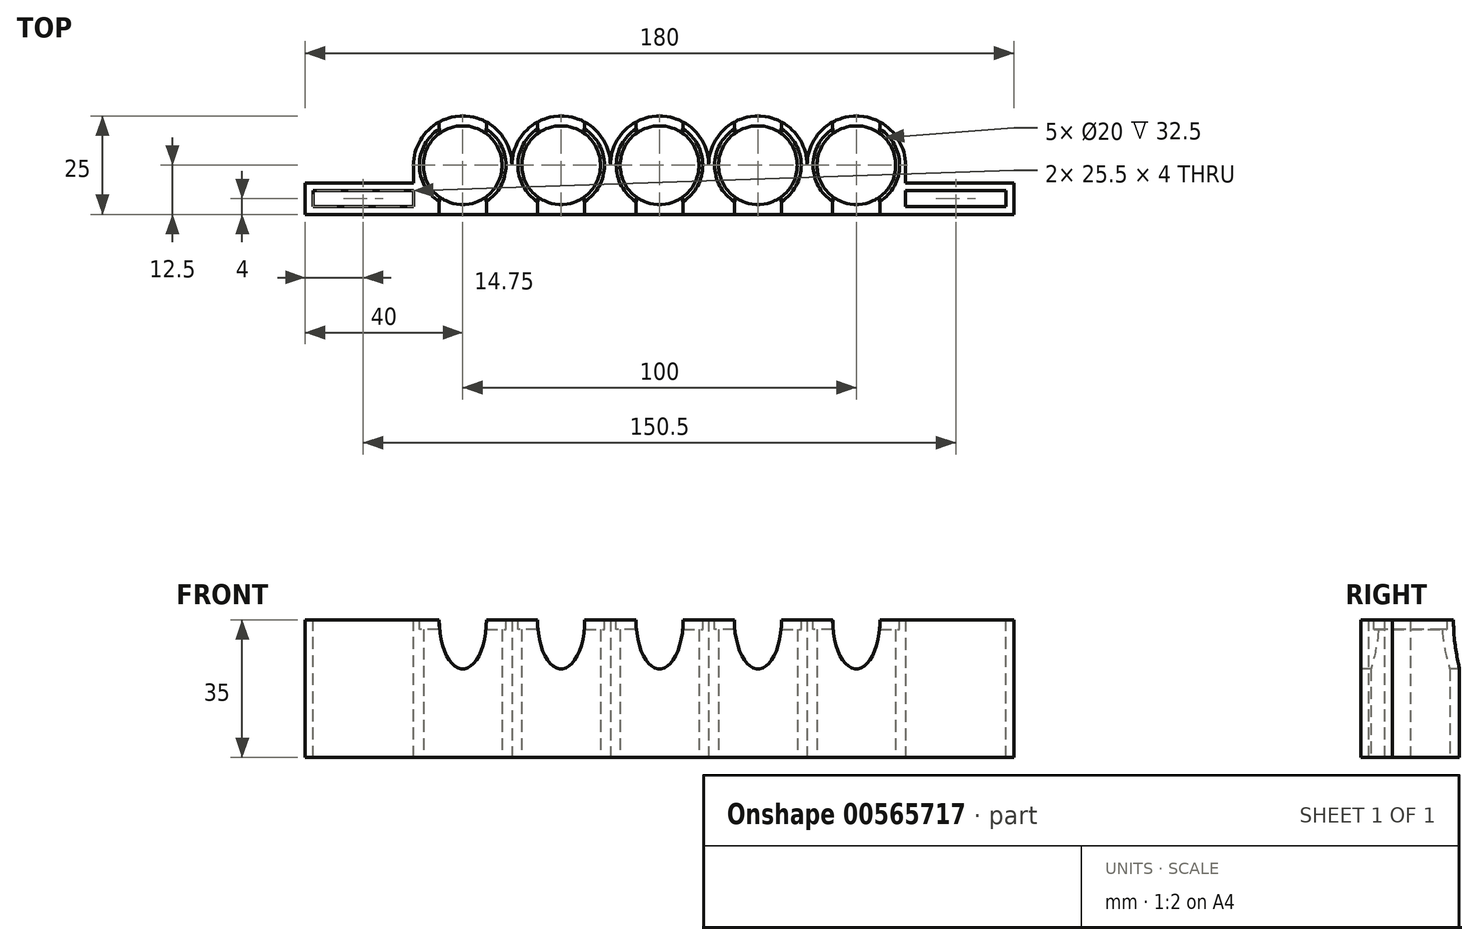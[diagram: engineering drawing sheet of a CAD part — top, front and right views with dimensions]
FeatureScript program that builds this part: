
annotation { "Feature Type Name" : "Feature", "Feature Type Description" : "" }
export const myFeature = defineFeature(function(context is Context, id is Id, definition is map)
    precondition{}
    {
        {
            var Q0;
            Q0=qCreatedBy(makeId("Top.planeOp"),FACE);
            var sketch = newSketch(context, id + "F0", { "sketchPlane" : qUnion([Q0])});
            skArc(sketch, "E0", {"start": v(12.5, 0) * mm, "mid": v(0, 12.5) * mm, "end": v(-12.5, 0) * mm});
            skArc(sketch, "E1.1.0.0", {"start": v(37.5, 0) * mm, "mid": v(25, 12.5) * mm, "end": v(12.5, 0) * mm});
            skArc(sketch, "E1.2.0.0", {"start": v(62.5, 0) * mm, "mid": v(50, 12.5) * mm, "end": v(37.5, 0) * mm});
            skArc(sketch, "E1.3.0.0", {"start": v(87.5, 0) * mm, "mid": v(75, 12.5) * mm, "end": v(62.5, 0) * mm});
            skArc(sketch, "E1.4.0.0", {"start": v(112.5, 0) * mm, "mid": v(100, 12.5) * mm, "end": v(87.5, 0) * mm});
            skLineSegment(sketch, "E1.direction1", {"start": v(0, 0) * mm, "end": v(25, 0) * mm, "construction": true});
            skLineSegment(sketch, "E2", {"start": v(-40, -12.5) * mm, "end": v(140, -12.5) * mm});
            skCircle(sketch, "E3", {"center": v(0, 0) * mm, "radius": 10 * mm});
            skCircle(sketch, "E4.1.0.0", {"center": v(25, 0) * mm, "radius": 10 * mm});
            skCircle(sketch, "E4.2.0.0", {"center": v(50, 0) * mm, "radius": 10 * mm});
            skCircle(sketch, "E4.3.0.0", {"center": v(75, 0) * mm, "radius": 10 * mm});
            skCircle(sketch, "E4.4.0.0", {"center": v(100, 0) * mm, "radius": 10 * mm});
            skLineSegment(sketch, "E5", {"start": v(-40, -12.5) * mm, "end": v(-40, -10.5) * mm});
            skLineSegment(sketch, "E6", {"start": v(-40, -10.5) * mm, "end": v(-12.5, -10.5) * mm});
            skLineSegment(sketch, "E7", {"start": v(140, -12.5) * mm, "end": v(140, -10.5) * mm});
            skLineSegment(sketch, "E8", {"start": v(140, -10.5) * mm, "end": v(112.5, -10.5) * mm});
            skPoint(sketch, "E9.orphan", {"position": v(0, -12.5) * mm});
            skLineSegment(sketch, "E10", {"start": v(-12.5, 0) * mm, "end": v(-12.5, -10.5) * mm});
            skLineSegment(sketch, "E11", {"start": v(112.5, 0) * mm, "end": v(112.5, -10.5) * mm});
            skPoint(sketch, "E12.orphan", {"position": v(100, -12.5) * mm});
            skSolve(sketch);
        }
        {
            var Q0;
            Q0 = qSketchRegion(id + "F0", true);
            extrude(context, id + "F1", {"entities" : qUnion([Q0]), "depth" : 35 * mm, "offsetDistance" : 25 * mm});
        }
        {
            var Q0;
            Q0=makeQuery(id+"F1.opExtrude","CAP_FACE",FACE,{"disambiguationData":[OSD([sQuery(id+"F0.wireOp",EDGE,"E0"),sQuery(id+"F0.wireOp",EDGE,"E1.1.0.0"),sQuery(id+"F0.wireOp",EDGE,"E1.2.0.0"),sQuery(id+"F0.wireOp",EDGE,"E1.3.0.0"),sQuery(id+"F0.wireOp",EDGE,"E1.4.0.0"),sQuery(id+"F0.wireOp",EDGE,"E2"),sQuery(id+"F0.wireOp",EDGE,"E3"),sQuery(id+"F0.wireOp",EDGE,"E4.1.0.0"),sQuery(id+"F0.wireOp",EDGE,"E4.2.0.0"),sQuery(id+"F0.wireOp",EDGE,"E4.3.0.0"),sQuery(id+"F0.wireOp",EDGE,"E4.4.0.0"),sQuery(id+"F0.wireOp",EDGE,"E5"),sQuery(id+"F0.wireOp",EDGE,"E6"),sQuery(id+"F0.wireOp",EDGE,"E7"),sQuery(id+"F0.wireOp",EDGE,"E8"),sQuery(id+"F0.wireOp",EDGE,"E10"),sQuery(id+"F0.wireOp",EDGE,"E11")])],"isStart":false});
            var sketch = newSketch(context, id + "F2", { "sketchPlane" : qUnion([Q0])});
            skCircle(sketch, "E13", {"center": v(0, 0) * mm, "radius": 11 * mm});
            skCircle(sketch, "E14.1.0.0", {"center": v(25, 0) * mm, "radius": 11 * mm});
            skCircle(sketch, "E14.2.0.0", {"center": v(50, 0) * mm, "radius": 11 * mm});
            skCircle(sketch, "E14.3.0.0", {"center": v(75, 0) * mm, "radius": 11 * mm});
            skCircle(sketch, "E14.4.0.0", {"center": v(100, 0) * mm, "radius": 11 * mm});
            skLineSegment(sketch, "E14.direction1", {"start": v(0, 0) * mm, "end": v(25, 0) * mm, "construction": true});
            skSolve(sketch);
        }
        {
            var Q0;
            Q0=makeQuery(id+"F2.imprint","IMPRINT",FACE,{"disambiguationData":[TD([[makeQuery(id+"F2.imprint","IMPRINT",EDGE,{"derivedFrom":sQuery(id+"F2.wireOp",EDGE,"E14.4.0.0")}),1.0]])]});
            var Q1;
            Q1=makeQuery(id+"F2.imprint","IMPRINT",FACE,{"disambiguationData":[TD([[makeQuery(id+"F2.imprint","IMPRINT",EDGE,{"derivedFrom":sQuery(id+"F2.wireOp",EDGE,"E14.3.0.0")}),1.0]])]});
            var Q2;
            Q2=makeQuery(id+"F2.imprint","IMPRINT",FACE,{"disambiguationData":[TD([[makeQuery(id+"F2.imprint","IMPRINT",EDGE,{"derivedFrom":makeQuery(id+"F1.opExtrude","CAP_EDGE",EDGE,{"disambiguationData":[OSD([sQuery(id+"F0.wireOp",EDGE,"E4.2.0.0")])],"isStart":false})}),1.0]])]});
            var Q3;
            Q3=makeQuery(id+"F2.imprint","IMPRINT",FACE,{"disambiguationData":[TD([[makeQuery(id+"F2.imprint","IMPRINT",EDGE,{"derivedFrom":sQuery(id+"F2.wireOp",EDGE,"E14.1.0.0")}),1.0]])]});
            var Q4;
            Q4=makeQuery(id+"F2.imprint","IMPRINT",FACE,{"disambiguationData":[TD([[makeQuery(id+"F2.imprint","IMPRINT",EDGE,{"derivedFrom":sQuery(id+"F2.wireOp",EDGE,"E13")}),1.0]])]});
            var Q5;
            Q5=makeQuery(id+"F2.imprint","IMPRINT",FACE,{"disambiguationData":[TD([[makeQuery(id+"F2.imprint","IMPRINT",EDGE,{"derivedFrom":sQuery(id+"F2.wireOp",EDGE,"E14.2.0.0")}),1.0]])]});
            var Q6;
            Q6=sQuery(id+"F2.wireOp",EDGE,"E14.4.0.0");
            extrude(context, id + "F3", {"entities" : qUnion([Q0, Q1, Q2, Q3, Q4, Q5]), "operationType" : NewBodyOperationType.REMOVE, "surfaceEntities" : qUnion([Q6]), "oppositeDirection" : true, "depth" : 2.5 * mm, "offsetDistance" : 25 * mm});
        }
        {
            var Q0;
            Q0=qCreatedBy(makeId("Front.planeOp"),FACE);
            var sketch = newSketch(context, id + "F4", { "sketchPlane" : qUnion([Q0])});
            skEllipse(sketch, "E15", {"center": v(0, 35) * mm, "majorRadius": 6 * mm, "minorRadius": 12.5 * mm, "majorAxis": v(-1, 0)});
            skEllipse(sketch, "E16.1.0.0", {"center": v(25, 35) * mm, "majorRadius": 6 * mm, "minorRadius": 12.5 * mm, "majorAxis": v(-1, 0)});
            skEllipse(sketch, "E16.2.0.0", {"center": v(50, 35) * mm, "majorRadius": 6 * mm, "minorRadius": 12.5 * mm, "majorAxis": v(-1, 0)});
            skEllipse(sketch, "E16.3.0.0", {"center": v(75, 35) * mm, "majorRadius": 6 * mm, "minorRadius": 12.5 * mm, "majorAxis": v(-1, 0)});
            skEllipse(sketch, "E16.4.0.0", {"center": v(100, 35) * mm, "majorRadius": 6 * mm, "minorRadius": 12.5 * mm, "majorAxis": v(-1, 0)});
            skLineSegment(sketch, "E16.direction1", {"start": v(0, 35) * mm, "end": v(25, 35) * mm, "construction": true});
            skSolve(sketch);
        }
        {
            var Q0;
            Q0=makeQuery(id+"F4.imprint","IMPRINT",FACE,{"disambiguationData":[TD([[makeQuery(id+"F4.imprint","IMPRINT",EDGE,{"derivedFrom":sQuery(id+"F4.wireOp",EDGE,"E15")}),1.0]])]});
            var Q1;
            Q1=makeQuery(id+"F4.imprint","IMPRINT",FACE,{"disambiguationData":[TD([[makeQuery(id+"F4.imprint","IMPRINT",EDGE,{"derivedFrom":sQuery(id+"F4.wireOp",EDGE,"E16.1.0.0")}),1.0]])]});
            var Q2;
            Q2=makeQuery(id+"F4.imprint","IMPRINT",FACE,{"disambiguationData":[TD([[makeQuery(id+"F4.imprint","IMPRINT",EDGE,{"derivedFrom":sQuery(id+"F4.wireOp",EDGE,"E16.2.0.0")}),1.0]])]});
            var Q3;
            Q3=makeQuery(id+"F4.imprint","IMPRINT",FACE,{"disambiguationData":[TD([[makeQuery(id+"F4.imprint","IMPRINT",EDGE,{"derivedFrom":sQuery(id+"F4.wireOp",EDGE,"E16.3.0.0")}),1.0]])]});
            var Q4;
            Q4=makeQuery(id+"F4.imprint","IMPRINT",FACE,{"disambiguationData":[TD([[makeQuery(id+"F4.imprint","IMPRINT",EDGE,{"derivedFrom":sQuery(id+"F4.wireOp",EDGE,"E16.4.0.0")}),1.0]])]});
            extrude(context, id + "F5", {"entities" : qUnion([Q0, Q1, Q2, Q3, Q4]), "operationType" : NewBodyOperationType.REMOVE, "endBound" : BoundingType.SYMMETRIC, "oppositeDirection" : true, "depth" : 50 * mm, "offsetDistance" : 25 * mm});
        }
        {
            var Q0;
            {var subQ0=sQuery(id+"F0.wireOp",EDGE,"E6");var subQ1=sQuery(id+"F0.wireOp",EDGE,"E5");var subQ2=sQuery(id+"F0.wireOp",EDGE,"E2");var subQ3=sQuery(id+"F0.wireOp",EDGE,"E0");var subQ4=sQuery(id+"F0.wireOp",EDGE,"E10");Q0=makeQuery(id+"F5.boolean.opBoolean","SPLIT",FACE,{"disambiguationData":[TD([makeQuery(id+"F1.opExtrude","SWEPT_FACE",FACE,{"disambiguationData":[OSD([subQ3])]}),makeQuery(id+"F1.opExtrude","SWEPT_FACE",FACE,{"disambiguationData":[OSD([subQ2])]}),makeQuery(id+"F1.opExtrude","SWEPT_FACE",FACE,{"disambiguationData":[OSD([subQ1])]}),makeQuery(id+"F1.opExtrude","SWEPT_FACE",FACE,{"disambiguationData":[OSD([subQ0])]}),makeQuery(id+"F1.opExtrude","SWEPT_FACE",FACE,{"disambiguationData":[OSD([subQ4])]}),makeQuery(id+"F3.boolean.opBoolean","COPY",FACE,{"derivedFrom":makeQuery(id+"F3.opExtrude","SWEPT_FACE",FACE,{"disambiguationData":[OSD([sQuery(id+"F2.wireOp",EDGE,"E13")])]})}),makeQuery(id+"F5.opExtrude","SWEPT_FACE",FACE,{"disambiguationData":[OSD([sQuery(id+"F4.wireOp",EDGE,"E15")])]})])],"derivedFrom":makeQuery(id+"F1.opExtrude","CAP_FACE",FACE,{"disambiguationData":[OSD([subQ3,sQuery(id+"F0.wireOp",EDGE,"E1.1.0.0"),sQuery(id+"F0.wireOp",EDGE,"E1.2.0.0"),sQuery(id+"F0.wireOp",EDGE,"E1.3.0.0"),sQuery(id+"F0.wireOp",EDGE,"E1.4.0.0"),subQ2,sQuery(id+"F0.wireOp",EDGE,"E3"),sQuery(id+"F0.wireOp",EDGE,"E4.1.0.0"),sQuery(id+"F0.wireOp",EDGE,"E4.2.0.0"),sQuery(id+"F0.wireOp",EDGE,"E4.3.0.0"),sQuery(id+"F0.wireOp",EDGE,"E4.4.0.0"),subQ1,subQ0,sQuery(id+"F0.wireOp",EDGE,"E7"),sQuery(id+"F0.wireOp",EDGE,"E8"),subQ4,sQuery(id+"F0.wireOp",EDGE,"E11")])],"isStart":false})});}
            var sketch = newSketch(context, id + "F6", { "sketchPlane" : qUnion([Q0])});
            skLineSegment(sketch, "E17.bottom", {"start": v(-12.5, -6.5) * mm, "end": v(-38, -6.5) * mm});
            skLineSegment(sketch, "E17.top", {"start": v(-12.5, -4.5) * mm, "end": v(-40, -4.5) * mm});
            skLineSegment(sketch, "E17.left", {"start": v(-12.5, -6.5) * mm, "end": v(-12.5, -4.5) * mm});
            skLineSegment(sketch, "E17.right", {"start": v(-40, -6.5) * mm, "end": v(-40, -4.5) * mm});
            skLineSegment(sketch, "E18.bottom", {"start": v(-38, -10.5) * mm, "end": v(-40, -10.5) * mm});
            skLineSegment(sketch, "E18.left", {"start": v(-38, -10.5) * mm, "end": v(-38, -6.5) * mm});
            skLineSegment(sketch, "E18.right", {"start": v(-40, -10.5) * mm, "end": v(-40, -6.5) * mm});
            skSolve(sketch);
        }
        {
            var Q0;
            Q0 = qSketchRegion(id + "F6", true);
            extrude(context, id + "F7", {"entities" : qUnion([Q0]), "operationType" : NewBodyOperationType.ADD, "oppositeDirection" : true, "depth" : 35 * mm, "offsetDistance" : 25 * mm});
        }
        {
            var Q0;
            {var subQ0=sQuery(id+"F0.wireOp",EDGE,"E7");var subQ1=sQuery(id+"F0.wireOp",EDGE,"E2");var subQ2=sQuery(id+"F0.wireOp",EDGE,"E11");var subQ3=sQuery(id+"F0.wireOp",EDGE,"E8");var subQ4=sQuery(id+"F0.wireOp",EDGE,"E1.4.0.0");Q0=makeQuery(id+"F5.boolean.opBoolean","SPLIT",FACE,{"disambiguationData":[TD([makeQuery(id+"F1.opExtrude","SWEPT_FACE",FACE,{"disambiguationData":[OSD([subQ4])]}),makeQuery(id+"F1.opExtrude","SWEPT_FACE",FACE,{"disambiguationData":[OSD([subQ1])]}),makeQuery(id+"F1.opExtrude","SWEPT_FACE",FACE,{"disambiguationData":[OSD([subQ0])]}),makeQuery(id+"F1.opExtrude","SWEPT_FACE",FACE,{"disambiguationData":[OSD([subQ3])]}),makeQuery(id+"F1.opExtrude","SWEPT_FACE",FACE,{"disambiguationData":[OSD([subQ2])]}),makeQuery(id+"F3.boolean.opBoolean","COPY",FACE,{"derivedFrom":makeQuery(id+"F3.opExtrude","SWEPT_FACE",FACE,{"disambiguationData":[OSD([sQuery(id+"F2.wireOp",EDGE,"E14.4.0.0")])]})}),makeQuery(id+"F5.opExtrude","SWEPT_FACE",FACE,{"disambiguationData":[OSD([sQuery(id+"F4.wireOp",EDGE,"E16.4.0.0")])]})])],"derivedFrom":makeQuery(id+"F1.opExtrude","CAP_FACE",FACE,{"disambiguationData":[OSD([sQuery(id+"F0.wireOp",EDGE,"E0"),sQuery(id+"F0.wireOp",EDGE,"E1.1.0.0"),sQuery(id+"F0.wireOp",EDGE,"E1.2.0.0"),sQuery(id+"F0.wireOp",EDGE,"E1.3.0.0"),subQ4,subQ1,sQuery(id+"F0.wireOp",EDGE,"E3"),sQuery(id+"F0.wireOp",EDGE,"E4.1.0.0"),sQuery(id+"F0.wireOp",EDGE,"E4.2.0.0"),sQuery(id+"F0.wireOp",EDGE,"E4.3.0.0"),sQuery(id+"F0.wireOp",EDGE,"E4.4.0.0"),sQuery(id+"F0.wireOp",EDGE,"E5"),sQuery(id+"F0.wireOp",EDGE,"E6"),subQ0,subQ3,sQuery(id+"F0.wireOp",EDGE,"E10"),subQ2])],"isStart":false})});}
            var sketch = newSketch(context, id + "F8", { "sketchPlane" : qUnion([Q0])});
            skLineSegment(sketch, "E19.bottom", {"start": v(112.5, -6.5) * mm, "end": v(138, -6.5) * mm});
            skLineSegment(sketch, "E19.top", {"start": v(112.5, -4.5) * mm, "end": v(140, -4.5) * mm});
            skLineSegment(sketch, "E19.left", {"start": v(112.5, -6.5) * mm, "end": v(112.5, -4.5) * mm});
            skLineSegment(sketch, "E19.right", {"start": v(140, -6.5) * mm, "end": v(140, -4.5) * mm});
            skLineSegment(sketch, "E20.bottom", {"start": v(140, -6.5) * mm, "end": v(138, -6.5) * mm});
            skLineSegment(sketch, "E20.top", {"start": v(140, -10.5) * mm, "end": v(138, -10.5) * mm});
            skLineSegment(sketch, "E20.left", {"start": v(140, -6.5) * mm, "end": v(140, -10.5) * mm});
            skLineSegment(sketch, "E20.right", {"start": v(138, -6.5) * mm, "end": v(138, -10.5) * mm});
            skSolve(sketch);
        }
        {
            var Q0;
            Q0 = qSketchRegion(id + "F8", true);
            extrude(context, id + "F9", {"entities" : qUnion([Q0]), "operationType" : NewBodyOperationType.ADD, "oppositeDirection" : true, "depth" : 35 * mm, "offsetDistance" : 25 * mm});
        }
    });
